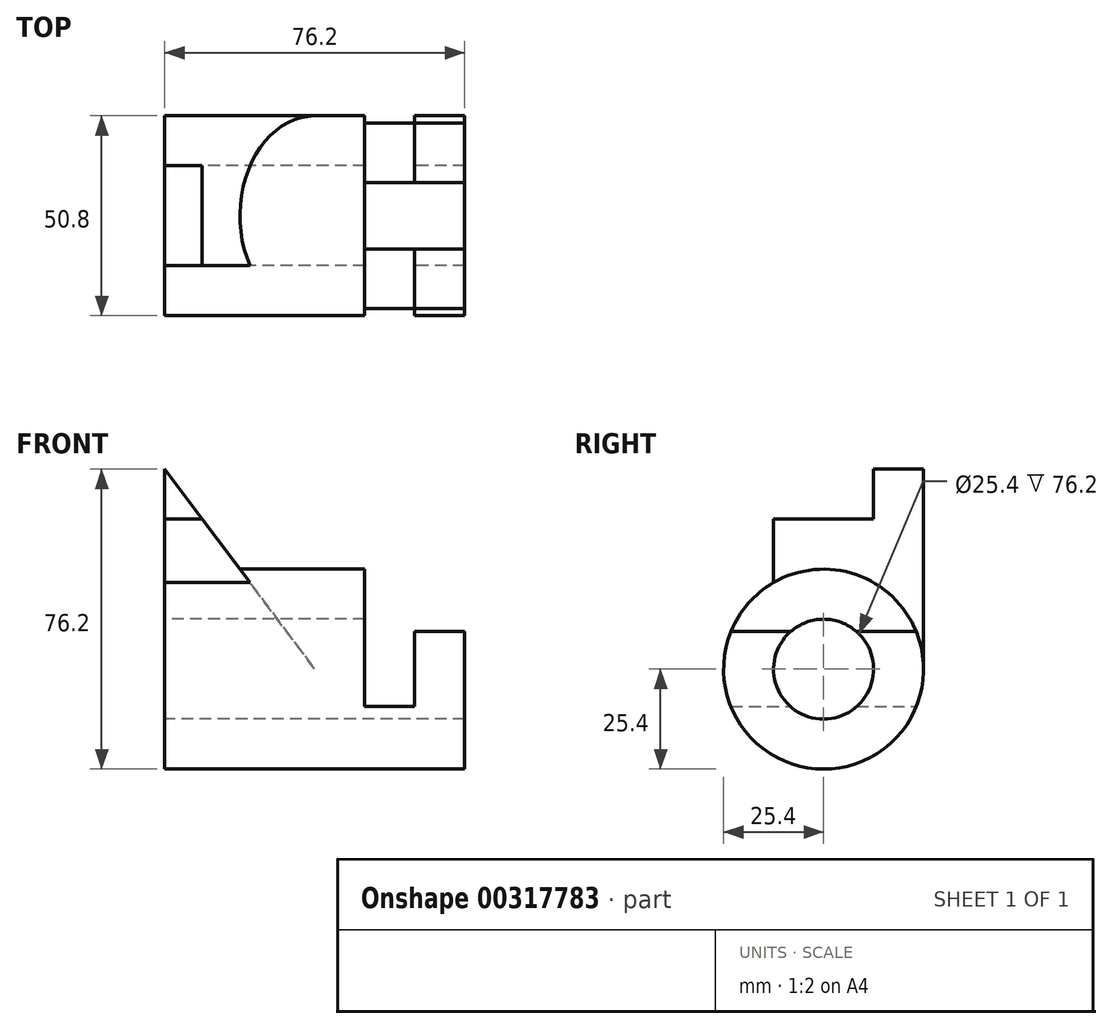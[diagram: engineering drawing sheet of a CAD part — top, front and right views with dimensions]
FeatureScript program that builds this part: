
annotation { "Feature Type Name" : "Feature", "Feature Type Description" : "" }
export const myFeature = defineFeature(function(context is Context, id is Id, definition is map)
    precondition{}
    {
        {
            var Q0;
            Q0=qCreatedBy(makeId("Front.planeOp"),FACE);
            var sketch = newSketch(context, id + "F0", { "sketchPlane" : qUnion([Q0])});
            skLineSegment(sketch, "E0", {"start": v(0, 0) * mm, "end": v(0, 50.8) * mm});
            skLineSegment(sketch, "E1", {"start": v(0, 0) * mm, "end": v(38.1, 0) * mm});
            skLineSegment(sketch, "E2", {"start": v(38.1, 0) * mm, "end": v(0, 50.8) * mm});
            skLineSegment(sketch, "E3", {"start": v(0, 38.1) * mm, "end": v(9.53, 38.1) * mm});
            skSolve(sketch);
        }
        {
            var Q0;
            {var subQ0=sQuery(id+"F0.wireOp",EDGE,"E1");Q0=makeQuery(id+"F0.imprint","IMPRINT",FACE,{"disambiguationData":[TD([[makeQuery(id+"F0.imprint","IMPRINT",EDGE,{"derivedFrom":subQ0}),1.0]])]});}
            extrude(context, id + "F1", {"entities" : qUnion([Q0]), "depth" : 38.1 * mm});
        }
        {
            var Q0;
            {var subQ3=sQuery(id+"F0.wireOp",EDGE,"E3");Q0=makeQuery(id+"F0.imprint","IMPRINT",FACE,{"disambiguationData":[TD([[makeQuery(id+"F0.imprint","IMPRINT",EDGE,{"derivedFrom":subQ3}),1.0]])]});}
            extrude(context, id + "F2", {"entities" : qUnion([Q0]), "operationType" : NewBodyOperationType.ADD, "depth" : 12.7 * mm});
        }
        {
            var Q0;
            {var subQ0=sQuery(id+"F0.wireOp",EDGE,"E0");Q0=makeQuery(id+"F2.boolean.opBoolean","MERGE",FACE,{"derivedFrom":[makeQuery(id+"F1.opExtrude","SWEPT_FACE",FACE,{"disambiguationData":[OSD([subQ0])]}),makeQuery(id+"F2.opExtrude","SWEPT_FACE",FACE,{"disambiguationData":[OSD([subQ0])]})]});}
            var sketch = newSketch(context, id + "F3", { "sketchPlane" : qUnion([Q0])});
            skCircle(sketch, "E4", {"center": v(25.4, 0) * mm, "radius": 25.4 * mm});
            skCircle(sketch, "E5", {"center": v(25.4, 0) * mm, "radius": 12.7 * mm});
            skSolve(sketch);
        }
        {
            var Q0;
            {var subQ0=sQuery(id+"F3.wireOp",EDGE,"E4");var subQ1=sQuery(id+"F0.wireOp",EDGE,"E0");var subQ4=makeQuery(id+"F1.opExtrude","CAP_EDGE",EDGE,{"disambiguationData":[OSD([subQ1])],"isStart":false});var subQ5=makeQuery(id+"F3.imprint","INTERSECT",VERTEX,{"derivedFrom":[subQ4,subQ0]});Q0=makeQuery(id+"F3.imprint","IMPRINT",FACE,{"disambiguationData":[TD([[makeQuery(id+"F3.imprint","IMPRINT",EDGE,{"disambiguationData":[TD([[subQ5,1.0]])],"derivedFrom":subQ4}),-1.0]])]});}
            var Q1;
            {var subQ0=sQuery(id+"F3.wireOp",EDGE,"E4");var subQ1=sQuery(id+"F0.wireOp",EDGE,"E0");var subQ4=makeQuery(id+"F1.opExtrude","CAP_EDGE",EDGE,{"disambiguationData":[OSD([subQ1])],"isStart":false});var subQ5=makeQuery(id+"F3.imprint","INTERSECT",VERTEX,{"derivedFrom":[subQ4,subQ0]});Q1=makeQuery(id+"F3.imprint","IMPRINT",FACE,{"disambiguationData":[TD([[makeQuery(id+"F3.imprint","IMPRINT",EDGE,{"disambiguationData":[TD([[subQ5,1.0]])],"derivedFrom":subQ4}),1.0]])]});}
            extrude(context, id + "F4", {"entities" : qUnion([Q0, Q1]), "operationType" : NewBodyOperationType.ADD, "oppositeDirection" : true, "depth" : 76.2 * mm});
        }
        {
            var Q0;
            {var subQ0=sQuery(id+"F3.wireOp",EDGE,"E5");var subQ1=sQuery(id+"F0.wireOp",EDGE,"E0");var subQ2=makeQuery(id+"F1.opExtrude","SWEPT_EDGE",EDGE,{"disambiguationData":[OSD([subQ1,sQuery(id+"F0.wireOp",EDGE,"E1")])]});var subQ4=makeQuery(id+"F3.imprint","INTERSECT",VERTEX,{"derivedFrom":[subQ2,subQ0]});Q0=makeQuery(id+"F3.imprint","IMPRINT",FACE,{"disambiguationData":[TD([[makeQuery(id+"F3.imprint","IMPRINT",EDGE,{"disambiguationData":[TD([[subQ4,1.0]])],"derivedFrom":subQ0}),1.0]])]});}
            extrude(context, id + "F5", {"entities" : qUnion([Q0]), "operationType" : NewBodyOperationType.REMOVE, "endBound" : BoundingType.THROUGH_ALL, "oppositeDirection" : true, "depth" : 25.4 * mm});
        }
        {
            var Q0;
            Q0=qCreatedBy(makeId("Front.planeOp"),FACE);
            var sketch = newSketch(context, id + "F6", { "sketchPlane" : qUnion([Q0])});
            skLineSegment(sketch, "E6", {"start": v(0, 0) * mm, "end": v(104.26, 0) * mm, "construction": true});
            skLineSegment(sketch, "E7", {"start": v(0, 0) * mm, "end": v(0, 25.4) * mm, "construction": true});
            skLineSegment(sketch, "E8", {"start": v(0, 25.4) * mm, "end": v(95.72, 25.4) * mm, "construction": true});
            skLineSegment(sketch, "E9", {"start": v(63.5, 25.4) * mm, "end": v(63.5, -9.53) * mm});
            skLineSegment(sketch, "E10", {"start": v(63.5, -9.52) * mm, "end": v(50.8, -9.52) * mm});
            skLineSegment(sketch, "E11", {"start": v(50.8, -9.53) * mm, "end": v(50.8, 25.4) * mm});
            skLineSegment(sketch, "E12", {"start": v(50.8, 25.4) * mm, "end": v(63.5, 25.4) * mm});
            skSolve(sketch);
        }
        {
            var Q0;
            Q0=makeQuery(id+"F6.imprint","IMPRINT",FACE,{"disambiguationData":[TD([[makeQuery(id+"F6.imprint","IMPRINT",EDGE,{"derivedFrom":sQuery(id+"F6.wireOp",EDGE,"E9")}),-1.0]])]});
            extrude(context, id + "F7", {"entities" : qUnion([Q0]), "operationType" : NewBodyOperationType.REMOVE, "endBound" : BoundingType.THROUGH_ALL, "depth" : 25.4 * mm});
        }
        {
            var Q0;
            Q0=makeQuery(id+"F4.opExtrude","CAP_FACE",FACE,{"disambiguationData":[OSD([sQuery(id+"F3.wireOp",EDGE,"E4"),sQuery(id+"F3.wireOp",EDGE,"E5")])],"isStart":false});
            var sketch = newSketch(context, id + "F8", { "sketchPlane" : qUnion([Q0])});
            skLineSegment(sketch, "E13", {"start": v(-25.4, 0) * mm, "end": v(-25.4, 9.53) * mm, "construction": true});
            skLineSegment(sketch, "E14", {"start": v(-25.4, 9.53) * mm, "end": v(-1.85, 9.53) * mm});
            skLineSegment(sketch, "E15", {"start": v(-25.4, 9.53) * mm, "end": v(-48.95, 9.53) * mm});
            skSolve(sketch);
        }
        {
            var Q0;
            {var subQ0=sQuery(id+"F8.wireOp",EDGE,"E14");var subQ1=makeQuery(id+"F4.opExtrude","CAP_EDGE",EDGE,{"disambiguationData":[OSD([sQuery(id+"F3.wireOp",EDGE,"E4")])],"isStart":false});var subQ2=makeQuery(id+"F8.imprint","INTERSECT",VERTEX,{"derivedFrom":[subQ1,subQ0]});Q0=makeQuery(id+"F8.imprint","IMPRINT",FACE,{"disambiguationData":[TD([[makeQuery(id+"F8.imprint","IMPRINT",EDGE,{"disambiguationData":[TD([[subQ2,1.0]])],"derivedFrom":subQ0}),1.0]])]});}
            var Q1;
            Q1=makeQuery(id+"F7.boolean.opBoolean","COPY",FACE,{"derivedFrom":makeQuery(id+"F7.opExtrude","SWEPT_FACE",FACE,{"disambiguationData":[OSD([sQuery(id+"F6.wireOp",EDGE,"E11")])]})});
            extrude(context, id + "F9", {"entities" : qUnion([Q0]), "operationType" : NewBodyOperationType.REMOVE, "endBound" : BoundingType.UP_TO_SURFACE, "oppositeDirection" : true, "endBoundEntityFace" : qUnion([Q1]), "depth" : 25.4 * mm});
        }
    });
